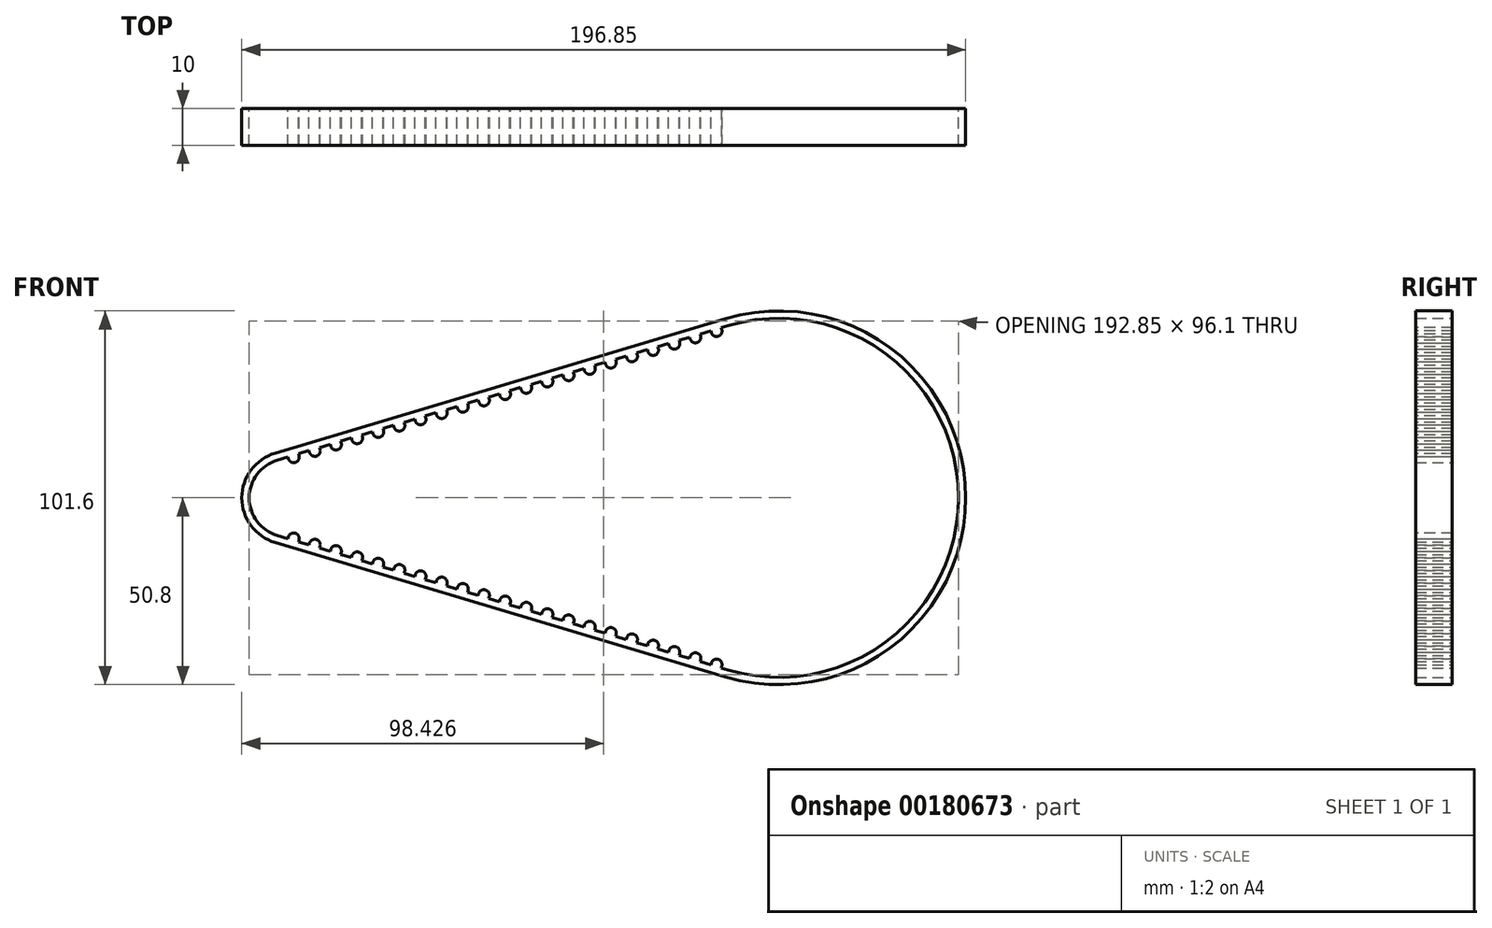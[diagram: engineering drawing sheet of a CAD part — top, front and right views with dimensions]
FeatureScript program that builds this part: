
annotation { "Feature Type Name" : "Feature", "Feature Type Description" : "" }
export const myFeature = defineFeature(function(context is Context, id is Id, definition is map)
    precondition{}
    {
        {
            var Q0;
            Q0=qCreatedBy(makeId("Front.planeOp"),FACE);
            var sketch = newSketch(context, id + "F0", { "sketchPlane" : qUnion([Q0])});
            skCircle(sketch, "E0", {"center": v(-282.88, 0) * mm, "radius": 30.69 * mm});
            skCircle(sketch, "E1", {"center": v(285.29, 0) * mm, "radius": 50.8 * mm});
            skLineSegment(sketch, "E2", {"start": v(-79.43, 12.17) * mm, "end": v(43.04, 48.68) * mm});
            skLineSegment(sketch, "E3", {"start": v(-79.43, -12.17) * mm, "end": v(43.04, -48.68) * mm});
            skArc(sketch, "E4", {"start": v(-79.43, 12.17) * mm, "mid": v(-88.5, 0) * mm, "end": v(-79.43, -12.17) * mm});
            skArc(sketch, "E5", {"start": v(43.04, -48.68) * mm, "mid": v(108.35, 0) * mm, "end": v(43.04, 48.68) * mm});
            skSolve(sketch);
        }
        {
            var Q0;
            Q0=makeQuery(id+"F0.imprint","IMPRINT",FACE,{"disambiguationData":[TD([[makeQuery(id+"F0.imprint","IMPRINT",EDGE,{"derivedFrom":sQuery(id+"F0.wireOp",EDGE,"E2")}),-1.0]])]});
            extrude(context, id + "F1", {"entities" : qUnion([Q0]), "depth" : 10 * mm});
        }
        {
            var Q0;
            Q0=makeQuery(id+"F1.opExtrude","CAP_FACE",FACE,{"disambiguationData":[OSD([sQuery(id+"F0.wireOp",EDGE,"E2"),sQuery(id+"F0.wireOp",EDGE,"E3"),sQuery(id+"F0.wireOp",EDGE,"E4"),sQuery(id+"F0.wireOp",EDGE,"E5")])],"isStart":false});
            var Q1;
            Q1=makeQuery(id+"F1.opExtrude","CAP_FACE",FACE,{"disambiguationData":[OSD([sQuery(id+"F0.wireOp",EDGE,"E2"),sQuery(id+"F0.wireOp",EDGE,"E3"),sQuery(id+"F0.wireOp",EDGE,"E4"),sQuery(id+"F0.wireOp",EDGE,"E5")])],"isStart":true});
            shell(context, id + "F2", {"entities" : qUnion([Q0, Q1]), "thickness" : 2 * mm});
        }
        {
            var Q0;
            Q0=makeQuery(id+"F1.opExtrude","SWEPT_FACE",FACE,{"disambiguationData":[OSD([sQuery(id+"F0.wireOp",EDGE,"E2")])]});
            var sketch = newSketch(context, id + "F3", { "sketchPlane" : qUnion([Q0])});
            skLineSegment(sketch, "E6", {"start": v(-69.64, 0) * mm, "end": v(-69.64, -10) * mm});
            skLineSegment(sketch, "E7", {"start": v(-72.64, -10) * mm, "end": v(-72.64, 0) * mm});
            skLineSegment(sketch, "E8", {"start": v(55.15, -10) * mm, "end": v(55.15, 0) * mm});
            skLineSegment(sketch, "E9.1.0.0", {"start": v(-66.64, 0) * mm, "end": v(-66.64, -10) * mm});
            skLineSegment(sketch, "E9.2.0.0", {"start": v(-63.64, 0) * mm, "end": v(-63.64, -10) * mm});
            skLineSegment(sketch, "E9.3.0.0", {"start": v(-60.64, 0) * mm, "end": v(-60.64, -10) * mm});
            skLineSegment(sketch, "E9.4.0.0", {"start": v(-57.64, 0) * mm, "end": v(-57.64, -10) * mm});
            skLineSegment(sketch, "E9.5.0.0", {"start": v(-54.64, 0) * mm, "end": v(-54.64, -10) * mm});
            skLineSegment(sketch, "E9.6.0.0", {"start": v(-51.64, 0) * mm, "end": v(-51.64, -10) * mm});
            skLineSegment(sketch, "E9.7.0.0", {"start": v(-48.64, 0) * mm, "end": v(-48.64, -10) * mm});
            skLineSegment(sketch, "E9.8.0.0", {"start": v(-45.64, 0) * mm, "end": v(-45.64, -10) * mm});
            skLineSegment(sketch, "E9.9.0.0", {"start": v(-42.64, 0) * mm, "end": v(-42.64, -10) * mm});
            skLineSegment(sketch, "E9.10.0.0", {"start": v(-39.64, 0) * mm, "end": v(-39.64, -10) * mm});
            skLineSegment(sketch, "E9.11.0.0", {"start": v(-36.64, 0) * mm, "end": v(-36.64, -10) * mm});
            skLineSegment(sketch, "E9.12.0.0", {"start": v(-33.64, 0) * mm, "end": v(-33.64, -10) * mm});
            skLineSegment(sketch, "E9.13.0.0", {"start": v(-30.64, 0) * mm, "end": v(-30.64, -10) * mm});
            skLineSegment(sketch, "E9.14.0.0", {"start": v(-27.64, 0) * mm, "end": v(-27.64, -10) * mm});
            skLineSegment(sketch, "E9.15.0.0", {"start": v(-24.64, 0) * mm, "end": v(-24.64, -10) * mm});
            skLineSegment(sketch, "E9.16.0.0", {"start": v(-21.64, 0) * mm, "end": v(-21.64, -10) * mm});
            skLineSegment(sketch, "E9.17.0.0", {"start": v(-18.64, 0) * mm, "end": v(-18.64, -10) * mm});
            skLineSegment(sketch, "E9.18.0.0", {"start": v(-15.64, 0) * mm, "end": v(-15.64, -10) * mm});
            skLineSegment(sketch, "E9.19.0.0", {"start": v(-12.64, 0) * mm, "end": v(-12.64, -10) * mm});
            skLineSegment(sketch, "E9.20.0.0", {"start": v(-9.64, 0) * mm, "end": v(-9.64, -10) * mm});
            skLineSegment(sketch, "E9.21.0.0", {"start": v(-6.64, 0) * mm, "end": v(-6.64, -10) * mm});
            skLineSegment(sketch, "E9.22.0.0", {"start": v(-3.64, 0) * mm, "end": v(-3.64, -10) * mm});
            skLineSegment(sketch, "E9.23.0.0", {"start": v(-0.64, 0) * mm, "end": v(-0.64, -10) * mm});
            skLineSegment(sketch, "E9.24.0.0", {"start": v(2.36, 0) * mm, "end": v(2.36, -10) * mm});
            skLineSegment(sketch, "E9.25.0.0", {"start": v(5.36, 0) * mm, "end": v(5.36, -10) * mm});
            skLineSegment(sketch, "E9.26.0.0", {"start": v(8.36, 0) * mm, "end": v(8.36, -10) * mm});
            skLineSegment(sketch, "E9.27.0.0", {"start": v(11.36, 0) * mm, "end": v(11.36, -10) * mm});
            skLineSegment(sketch, "E9.28.0.0", {"start": v(14.36, 0) * mm, "end": v(14.36, -10) * mm});
            skLineSegment(sketch, "E9.29.0.0", {"start": v(17.36, 0) * mm, "end": v(17.36, -10) * mm});
            skLineSegment(sketch, "E9.30.0.0", {"start": v(20.36, 0) * mm, "end": v(20.36, -10) * mm});
            skLineSegment(sketch, "E9.31.0.0", {"start": v(23.36, 0) * mm, "end": v(23.36, -10) * mm});
            skLineSegment(sketch, "E9.32.0.0", {"start": v(26.36, 0) * mm, "end": v(26.36, -10) * mm});
            skLineSegment(sketch, "E9.33.0.0", {"start": v(29.36, 0) * mm, "end": v(29.36, -10) * mm});
            skLineSegment(sketch, "E9.34.0.0", {"start": v(32.36, 0) * mm, "end": v(32.36, -10) * mm});
            skLineSegment(sketch, "E9.35.0.0", {"start": v(35.36, 0) * mm, "end": v(35.36, -10) * mm});
            skLineSegment(sketch, "E9.36.0.0", {"start": v(38.36, 0) * mm, "end": v(38.36, -10) * mm});
            skLineSegment(sketch, "E9.37.0.0", {"start": v(41.36, 0) * mm, "end": v(41.36, -10) * mm});
            skLineSegment(sketch, "E9.38.0.0", {"start": v(44.36, 0) * mm, "end": v(44.36, -10) * mm});
            skLineSegment(sketch, "E9.39.0.0", {"start": v(47.36, 0) * mm, "end": v(47.36, -10) * mm});
            skLineSegment(sketch, "E9.40.0.0", {"start": v(50.36, 0) * mm, "end": v(50.36, -10) * mm});
            skLineSegment(sketch, "E9.41.0.0", {"start": v(53.36, 0) * mm, "end": v(53.36, -10) * mm});
            skLineSegment(sketch, "E9.direction1", {"start": v(-69.64, -10) * mm, "end": v(-66.64, -10) * mm, "construction": true});
            skSolve(sketch);
        }
        {
            var Q0;
            {var subQ0=sQuery(id+"F3.wireOp",EDGE,"E6");Q0=makeQuery(id+"F3.imprint","IMPRINT",FACE,{"disambiguationData":[TD([[makeQuery(id+"F3.imprint","IMPRINT",EDGE,{"derivedFrom":subQ0}),1.0]])]});}
            var Q1;
            {var subQ0=sQuery(id+"F3.wireOp",EDGE,"E9.2.0.0");Q1=makeQuery(id+"F3.imprint","IMPRINT",FACE,{"disambiguationData":[TD([[makeQuery(id+"F3.imprint","IMPRINT",EDGE,{"derivedFrom":subQ0}),1.0]])]});}
            var Q2;
            {var subQ0=sQuery(id+"F3.wireOp",EDGE,"E9.4.0.0");Q2=makeQuery(id+"F3.imprint","IMPRINT",FACE,{"disambiguationData":[TD([[makeQuery(id+"F3.imprint","IMPRINT",EDGE,{"derivedFrom":subQ0}),1.0]])]});}
            var Q3;
            {var subQ0=sQuery(id+"F3.wireOp",EDGE,"E9.6.0.0");Q3=makeQuery(id+"F3.imprint","IMPRINT",FACE,{"disambiguationData":[TD([[makeQuery(id+"F3.imprint","IMPRINT",EDGE,{"derivedFrom":subQ0}),1.0]])]});}
            var Q4;
            {var subQ0=sQuery(id+"F3.wireOp",EDGE,"E9.8.0.0");Q4=makeQuery(id+"F3.imprint","IMPRINT",FACE,{"disambiguationData":[TD([[makeQuery(id+"F3.imprint","IMPRINT",EDGE,{"derivedFrom":subQ0}),1.0]])]});}
            var Q5;
            {var subQ0=sQuery(id+"F3.wireOp",EDGE,"E9.10.0.0");Q5=makeQuery(id+"F3.imprint","IMPRINT",FACE,{"disambiguationData":[TD([[makeQuery(id+"F3.imprint","IMPRINT",EDGE,{"derivedFrom":subQ0}),1.0]])]});}
            var Q6;
            {var subQ0=sQuery(id+"F3.wireOp",EDGE,"E9.12.0.0");Q6=makeQuery(id+"F3.imprint","IMPRINT",FACE,{"disambiguationData":[TD([[makeQuery(id+"F3.imprint","IMPRINT",EDGE,{"derivedFrom":subQ0}),1.0]])]});}
            var Q7;
            {var subQ0=sQuery(id+"F3.wireOp",EDGE,"E9.14.0.0");Q7=makeQuery(id+"F3.imprint","IMPRINT",FACE,{"disambiguationData":[TD([[makeQuery(id+"F3.imprint","IMPRINT",EDGE,{"derivedFrom":subQ0}),1.0]])]});}
            var Q8;
            {var subQ0=sQuery(id+"F3.wireOp",EDGE,"E9.16.0.0");Q8=makeQuery(id+"F3.imprint","IMPRINT",FACE,{"disambiguationData":[TD([[makeQuery(id+"F3.imprint","IMPRINT",EDGE,{"derivedFrom":subQ0}),1.0]])]});}
            var Q9;
            {var subQ0=sQuery(id+"F3.wireOp",EDGE,"E9.18.0.0");Q9=makeQuery(id+"F3.imprint","IMPRINT",FACE,{"disambiguationData":[TD([[makeQuery(id+"F3.imprint","IMPRINT",EDGE,{"derivedFrom":subQ0}),1.0]])]});}
            var Q10;
            {var subQ0=sQuery(id+"F3.wireOp",EDGE,"E9.20.0.0");Q10=makeQuery(id+"F3.imprint","IMPRINT",FACE,{"disambiguationData":[TD([[makeQuery(id+"F3.imprint","IMPRINT",EDGE,{"derivedFrom":subQ0}),1.0]])]});}
            var Q11;
            {var subQ0=sQuery(id+"F3.wireOp",EDGE,"E9.22.0.0");Q11=makeQuery(id+"F3.imprint","IMPRINT",FACE,{"disambiguationData":[TD([[makeQuery(id+"F3.imprint","IMPRINT",EDGE,{"derivedFrom":subQ0}),1.0]])]});}
            var Q12;
            {var subQ0=sQuery(id+"F3.wireOp",EDGE,"E9.24.0.0");Q12=makeQuery(id+"F3.imprint","IMPRINT",FACE,{"disambiguationData":[TD([[makeQuery(id+"F3.imprint","IMPRINT",EDGE,{"derivedFrom":subQ0}),1.0]])]});}
            var Q13;
            {var subQ0=sQuery(id+"F3.wireOp",EDGE,"E9.26.0.0");Q13=makeQuery(id+"F3.imprint","IMPRINT",FACE,{"disambiguationData":[TD([[makeQuery(id+"F3.imprint","IMPRINT",EDGE,{"derivedFrom":subQ0}),1.0]])]});}
            var Q14;
            {var subQ0=sQuery(id+"F3.wireOp",EDGE,"E9.28.0.0");Q14=makeQuery(id+"F3.imprint","IMPRINT",FACE,{"disambiguationData":[TD([[makeQuery(id+"F3.imprint","IMPRINT",EDGE,{"derivedFrom":subQ0}),1.0]])]});}
            var Q15;
            {var subQ0=sQuery(id+"F3.wireOp",EDGE,"E9.30.0.0");Q15=makeQuery(id+"F3.imprint","IMPRINT",FACE,{"disambiguationData":[TD([[makeQuery(id+"F3.imprint","IMPRINT",EDGE,{"derivedFrom":subQ0}),1.0]])]});}
            var Q16;
            {var subQ0=sQuery(id+"F3.wireOp",EDGE,"E9.32.0.0");Q16=makeQuery(id+"F3.imprint","IMPRINT",FACE,{"disambiguationData":[TD([[makeQuery(id+"F3.imprint","IMPRINT",EDGE,{"derivedFrom":subQ0}),1.0]])]});}
            var Q17;
            {var subQ0=sQuery(id+"F3.wireOp",EDGE,"E9.34.0.0");Q17=makeQuery(id+"F3.imprint","IMPRINT",FACE,{"disambiguationData":[TD([[makeQuery(id+"F3.imprint","IMPRINT",EDGE,{"derivedFrom":subQ0}),1.0]])]});}
            var Q18;
            {var subQ0=sQuery(id+"F3.wireOp",EDGE,"E9.36.0.0");Q18=makeQuery(id+"F3.imprint","IMPRINT",FACE,{"disambiguationData":[TD([[makeQuery(id+"F3.imprint","IMPRINT",EDGE,{"derivedFrom":subQ0}),1.0]])]});}
            var Q19;
            {var subQ0=sQuery(id+"F3.wireOp",EDGE,"E9.38.0.0");Q19=makeQuery(id+"F3.imprint","IMPRINT",FACE,{"disambiguationData":[TD([[makeQuery(id+"F3.imprint","IMPRINT",EDGE,{"derivedFrom":subQ0}),1.0]])]});}
            var Q20;
            {var subQ0=sQuery(id+"F3.wireOp",EDGE,"E9.40.0.0");Q20=makeQuery(id+"F3.imprint","IMPRINT",FACE,{"disambiguationData":[TD([[makeQuery(id+"F3.imprint","IMPRINT",EDGE,{"derivedFrom":subQ0}),1.0]])]});}
            extrude(context, id + "F4", {"entities" : qUnion([Q0, Q1, Q2, Q3, Q4, Q5, Q6, Q7, Q8, Q9, Q10, Q11, Q12, Q13, Q14, Q15, Q16, Q17, Q18, Q19, Q20]), "operationType" : NewBodyOperationType.ADD, "oppositeDirection" : true, "depth" : 4 * mm});
        }
        {
            var Q0;
            Q0=makeQuery(id+"F4.opExtrude","CAP_EDGE",EDGE,{"disambiguationData":[OSD([sQuery(id+"F3.wireOp",EDGE,"E6")])],"isStart":false});
            fillet(context, id + "F5", {"entities" : qUnion([Q0]), "radius" : 1.5 * mm, "tangentPropagation" : true, "allowEdgeOverflow" : false});
        }
        {
            var Q0;
            Q0=makeQuery(id+"F4.opExtrude","CAP_EDGE",EDGE,{"disambiguationData":[OSD([sQuery(id+"F3.wireOp",EDGE,"E9.1.0.0")])],"isStart":false});
            var Q1;
            Q1=makeQuery(id+"F4.opExtrude","CAP_EDGE",EDGE,{"disambiguationData":[OSD([sQuery(id+"F3.wireOp",EDGE,"E9.2.0.0")])],"isStart":false});
            var Q2;
            Q2=makeQuery(id+"F4.opExtrude","CAP_EDGE",EDGE,{"disambiguationData":[OSD([sQuery(id+"F3.wireOp",EDGE,"E9.3.0.0")])],"isStart":false});
            var Q3;
            Q3=makeQuery(id+"F4.opExtrude","CAP_EDGE",EDGE,{"disambiguationData":[OSD([sQuery(id+"F3.wireOp",EDGE,"E9.4.0.0")])],"isStart":false});
            var Q4;
            Q4=makeQuery(id+"F4.opExtrude","CAP_EDGE",EDGE,{"disambiguationData":[OSD([sQuery(id+"F3.wireOp",EDGE,"E9.5.0.0")])],"isStart":false});
            var Q5;
            Q5=makeQuery(id+"F4.opExtrude","CAP_EDGE",EDGE,{"disambiguationData":[OSD([sQuery(id+"F3.wireOp",EDGE,"E9.6.0.0")])],"isStart":false});
            var Q6;
            Q6=makeQuery(id+"F4.opExtrude","CAP_EDGE",EDGE,{"disambiguationData":[OSD([sQuery(id+"F3.wireOp",EDGE,"E9.7.0.0")])],"isStart":false});
            var Q7;
            Q7=makeQuery(id+"F4.opExtrude","CAP_EDGE",EDGE,{"disambiguationData":[OSD([sQuery(id+"F3.wireOp",EDGE,"E9.8.0.0")])],"isStart":false});
            var Q8;
            Q8=makeQuery(id+"F4.opExtrude","CAP_EDGE",EDGE,{"disambiguationData":[OSD([sQuery(id+"F3.wireOp",EDGE,"E9.9.0.0")])],"isStart":false});
            var Q9;
            Q9=makeQuery(id+"F4.opExtrude","CAP_EDGE",EDGE,{"disambiguationData":[OSD([sQuery(id+"F3.wireOp",EDGE,"E9.10.0.0")])],"isStart":false});
            var Q10;
            Q10=makeQuery(id+"F4.opExtrude","CAP_EDGE",EDGE,{"disambiguationData":[OSD([sQuery(id+"F3.wireOp",EDGE,"E9.11.0.0")])],"isStart":false});
            var Q11;
            Q11=makeQuery(id+"F4.opExtrude","CAP_EDGE",EDGE,{"disambiguationData":[OSD([sQuery(id+"F3.wireOp",EDGE,"E9.12.0.0")])],"isStart":false});
            var Q12;
            Q12=makeQuery(id+"F4.opExtrude","CAP_EDGE",EDGE,{"disambiguationData":[OSD([sQuery(id+"F3.wireOp",EDGE,"E9.13.0.0")])],"isStart":false});
            var Q13;
            Q13=makeQuery(id+"F4.opExtrude","CAP_EDGE",EDGE,{"disambiguationData":[OSD([sQuery(id+"F3.wireOp",EDGE,"E9.14.0.0")])],"isStart":false});
            var Q14;
            Q14=makeQuery(id+"F4.opExtrude","CAP_EDGE",EDGE,{"disambiguationData":[OSD([sQuery(id+"F3.wireOp",EDGE,"E9.15.0.0")])],"isStart":false});
            var Q15;
            Q15=makeQuery(id+"F4.opExtrude","CAP_EDGE",EDGE,{"disambiguationData":[OSD([sQuery(id+"F3.wireOp",EDGE,"E9.16.0.0")])],"isStart":false});
            var Q16;
            Q16=makeQuery(id+"F4.opExtrude","CAP_EDGE",EDGE,{"disambiguationData":[OSD([sQuery(id+"F3.wireOp",EDGE,"E9.17.0.0")])],"isStart":false});
            var Q17;
            Q17=makeQuery(id+"F4.opExtrude","CAP_EDGE",EDGE,{"disambiguationData":[OSD([sQuery(id+"F3.wireOp",EDGE,"E9.18.0.0")])],"isStart":false});
            var Q18;
            Q18=makeQuery(id+"F4.opExtrude","CAP_EDGE",EDGE,{"disambiguationData":[OSD([sQuery(id+"F3.wireOp",EDGE,"E9.19.0.0")])],"isStart":false});
            var Q19;
            Q19=makeQuery(id+"F4.opExtrude","CAP_EDGE",EDGE,{"disambiguationData":[OSD([sQuery(id+"F3.wireOp",EDGE,"E9.20.0.0")])],"isStart":false});
            var Q20;
            Q20=makeQuery(id+"F4.opExtrude","CAP_EDGE",EDGE,{"disambiguationData":[OSD([sQuery(id+"F3.wireOp",EDGE,"E9.21.0.0")])],"isStart":false});
            var Q21;
            Q21=makeQuery(id+"F4.opExtrude","CAP_EDGE",EDGE,{"disambiguationData":[OSD([sQuery(id+"F3.wireOp",EDGE,"E9.22.0.0")])],"isStart":false});
            var Q22;
            Q22=makeQuery(id+"F4.opExtrude","CAP_EDGE",EDGE,{"disambiguationData":[OSD([sQuery(id+"F3.wireOp",EDGE,"E9.23.0.0")])],"isStart":false});
            var Q23;
            Q23=makeQuery(id+"F4.opExtrude","CAP_EDGE",EDGE,{"disambiguationData":[OSD([sQuery(id+"F3.wireOp",EDGE,"E9.24.0.0")])],"isStart":false});
            var Q24;
            Q24=makeQuery(id+"F4.opExtrude","CAP_EDGE",EDGE,{"disambiguationData":[OSD([sQuery(id+"F3.wireOp",EDGE,"E9.25.0.0")])],"isStart":false});
            var Q25;
            Q25=makeQuery(id+"F4.opExtrude","CAP_EDGE",EDGE,{"disambiguationData":[OSD([sQuery(id+"F3.wireOp",EDGE,"E9.26.0.0")])],"isStart":false});
            var Q26;
            Q26=makeQuery(id+"F4.opExtrude","CAP_EDGE",EDGE,{"disambiguationData":[OSD([sQuery(id+"F3.wireOp",EDGE,"E9.27.0.0")])],"isStart":false});
            var Q27;
            Q27=makeQuery(id+"F4.opExtrude","CAP_EDGE",EDGE,{"disambiguationData":[OSD([sQuery(id+"F3.wireOp",EDGE,"E9.28.0.0")])],"isStart":false});
            var Q28;
            Q28=makeQuery(id+"F4.opExtrude","CAP_EDGE",EDGE,{"disambiguationData":[OSD([sQuery(id+"F3.wireOp",EDGE,"E9.29.0.0")])],"isStart":false});
            var Q29;
            Q29=makeQuery(id+"F4.opExtrude","CAP_EDGE",EDGE,{"disambiguationData":[OSD([sQuery(id+"F3.wireOp",EDGE,"E9.30.0.0")])],"isStart":false});
            var Q30;
            Q30=makeQuery(id+"F4.opExtrude","CAP_EDGE",EDGE,{"disambiguationData":[OSD([sQuery(id+"F3.wireOp",EDGE,"E9.31.0.0")])],"isStart":false});
            var Q31;
            Q31=makeQuery(id+"F4.opExtrude","CAP_EDGE",EDGE,{"disambiguationData":[OSD([sQuery(id+"F3.wireOp",EDGE,"E9.32.0.0")])],"isStart":false});
            var Q32;
            Q32=makeQuery(id+"F4.opExtrude","CAP_EDGE",EDGE,{"disambiguationData":[OSD([sQuery(id+"F3.wireOp",EDGE,"E9.33.0.0")])],"isStart":false});
            var Q33;
            Q33=makeQuery(id+"F4.opExtrude","CAP_EDGE",EDGE,{"disambiguationData":[OSD([sQuery(id+"F3.wireOp",EDGE,"E9.34.0.0")])],"isStart":false});
            var Q34;
            Q34=makeQuery(id+"F4.opExtrude","CAP_EDGE",EDGE,{"disambiguationData":[OSD([sQuery(id+"F3.wireOp",EDGE,"E9.35.0.0")])],"isStart":false});
            var Q35;
            Q35=makeQuery(id+"F4.opExtrude","CAP_EDGE",EDGE,{"disambiguationData":[OSD([sQuery(id+"F3.wireOp",EDGE,"E9.36.0.0")])],"isStart":false});
            var Q36;
            Q36=makeQuery(id+"F4.opExtrude","CAP_EDGE",EDGE,{"disambiguationData":[OSD([sQuery(id+"F3.wireOp",EDGE,"E9.37.0.0")])],"isStart":false});
            var Q37;
            Q37=makeQuery(id+"F4.opExtrude","CAP_EDGE",EDGE,{"disambiguationData":[OSD([sQuery(id+"F3.wireOp",EDGE,"E9.38.0.0")])],"isStart":false});
            var Q38;
            Q38=makeQuery(id+"F4.opExtrude","CAP_EDGE",EDGE,{"disambiguationData":[OSD([sQuery(id+"F3.wireOp",EDGE,"E9.39.0.0")])],"isStart":false});
            var Q39;
            Q39=makeQuery(id+"F4.opExtrude","CAP_EDGE",EDGE,{"disambiguationData":[OSD([sQuery(id+"F3.wireOp",EDGE,"E9.40.0.0")])],"isStart":false});
            var Q40;
            Q40=makeQuery(id+"F4.opExtrude","CAP_EDGE",EDGE,{"disambiguationData":[OSD([sQuery(id+"F3.wireOp",EDGE,"E9.41.0.0")])],"isStart":false});
            fillet(context, id + "F6", {"entities" : qUnion([Q0, Q1, Q2, Q3, Q4, Q5, Q6, Q7, Q8, Q9, Q10, Q11, Q12, Q13, Q14, Q15, Q16, Q17, Q18, Q19, Q20, Q21, Q22, Q23, Q24, Q25, Q26, Q27, Q28, Q29, Q30, Q31, Q32, Q33, Q34, Q35, Q36, Q37, Q38, Q39, Q40]), "radius" : 1.5 * mm, "tangentPropagation" : true, "allowEdgeOverflow" : false});
        }
        {
            var Q0;
            Q0=makeQuery(id+"F1.opExtrude","SWEPT_FACE",FACE,{"disambiguationData":[OSD([sQuery(id+"F0.wireOp",EDGE,"E3")])]});
            var sketch = newSketch(context, id + "F7", { "sketchPlane" : qUnion([Q0])});
            skLineSegment(sketch, "E10", {"start": v(-72.64, 0) * mm, "end": v(-72.64, 10) * mm});
            skLineSegment(sketch, "E11", {"start": v(-69.64, 0) * mm, "end": v(-69.64, 10) * mm});
            skLineSegment(sketch, "E12.1.0.0", {"start": v(-66.64, 0) * mm, "end": v(-66.64, 10) * mm});
            skLineSegment(sketch, "E12.2.0.0", {"start": v(-63.64, 0) * mm, "end": v(-63.64, 10) * mm});
            skLineSegment(sketch, "E12.3.0.0", {"start": v(-60.64, 0) * mm, "end": v(-60.64, 10) * mm});
            skLineSegment(sketch, "E12.4.0.0", {"start": v(-57.64, 0) * mm, "end": v(-57.64, 10) * mm});
            skLineSegment(sketch, "E12.5.0.0", {"start": v(-54.64, 0) * mm, "end": v(-54.64, 10) * mm});
            skLineSegment(sketch, "E12.6.0.0", {"start": v(-51.64, 0) * mm, "end": v(-51.64, 10) * mm});
            skLineSegment(sketch, "E12.7.0.0", {"start": v(-48.64, 0) * mm, "end": v(-48.64, 10) * mm});
            skLineSegment(sketch, "E12.8.0.0", {"start": v(-45.64, 0) * mm, "end": v(-45.64, 10) * mm});
            skLineSegment(sketch, "E12.9.0.0", {"start": v(-42.64, 0) * mm, "end": v(-42.64, 10) * mm});
            skLineSegment(sketch, "E12.10.0.0", {"start": v(-39.64, 0) * mm, "end": v(-39.64, 10) * mm});
            skLineSegment(sketch, "E12.11.0.0", {"start": v(-36.64, 0) * mm, "end": v(-36.64, 10) * mm});
            skLineSegment(sketch, "E12.12.0.0", {"start": v(-33.64, 0) * mm, "end": v(-33.64, 10) * mm});
            skLineSegment(sketch, "E12.13.0.0", {"start": v(-30.64, 0) * mm, "end": v(-30.64, 10) * mm});
            skLineSegment(sketch, "E12.14.0.0", {"start": v(-27.64, 0) * mm, "end": v(-27.64, 10) * mm});
            skLineSegment(sketch, "E12.15.0.0", {"start": v(-24.64, 0) * mm, "end": v(-24.64, 10) * mm});
            skLineSegment(sketch, "E12.16.0.0", {"start": v(-21.64, 0) * mm, "end": v(-21.64, 10) * mm});
            skLineSegment(sketch, "E12.17.0.0", {"start": v(-18.64, 0) * mm, "end": v(-18.64, 10) * mm});
            skLineSegment(sketch, "E12.18.0.0", {"start": v(-15.64, 0) * mm, "end": v(-15.64, 10) * mm});
            skLineSegment(sketch, "E12.19.0.0", {"start": v(-12.64, 0) * mm, "end": v(-12.64, 10) * mm});
            skLineSegment(sketch, "E12.20.0.0", {"start": v(-9.64, 0) * mm, "end": v(-9.64, 10) * mm});
            skLineSegment(sketch, "E12.21.0.0", {"start": v(-6.64, 0) * mm, "end": v(-6.64, 10) * mm});
            skLineSegment(sketch, "E12.22.0.0", {"start": v(-3.64, 0) * mm, "end": v(-3.64, 10) * mm});
            skLineSegment(sketch, "E12.23.0.0", {"start": v(-0.64, 0) * mm, "end": v(-0.64, 10) * mm});
            skLineSegment(sketch, "E12.24.0.0", {"start": v(2.36, 0) * mm, "end": v(2.36, 10) * mm});
            skLineSegment(sketch, "E12.25.0.0", {"start": v(5.36, 0) * mm, "end": v(5.36, 10) * mm});
            skLineSegment(sketch, "E12.26.0.0", {"start": v(8.36, 0) * mm, "end": v(8.36, 10) * mm});
            skLineSegment(sketch, "E12.27.0.0", {"start": v(11.36, 0) * mm, "end": v(11.36, 10) * mm});
            skLineSegment(sketch, "E12.28.0.0", {"start": v(14.36, 0) * mm, "end": v(14.36, 10) * mm});
            skLineSegment(sketch, "E12.29.0.0", {"start": v(17.36, 0) * mm, "end": v(17.36, 10) * mm});
            skLineSegment(sketch, "E12.30.0.0", {"start": v(20.36, 0) * mm, "end": v(20.36, 10) * mm});
            skLineSegment(sketch, "E12.31.0.0", {"start": v(23.36, 0) * mm, "end": v(23.36, 10) * mm});
            skLineSegment(sketch, "E12.32.0.0", {"start": v(26.36, 0) * mm, "end": v(26.36, 10) * mm});
            skLineSegment(sketch, "E12.33.0.0", {"start": v(29.36, 0) * mm, "end": v(29.36, 10) * mm});
            skLineSegment(sketch, "E12.34.0.0", {"start": v(32.36, 0) * mm, "end": v(32.36, 10) * mm});
            skLineSegment(sketch, "E12.35.0.0", {"start": v(35.36, 0) * mm, "end": v(35.36, 10) * mm});
            skLineSegment(sketch, "E12.36.0.0", {"start": v(38.36, 0) * mm, "end": v(38.36, 10) * mm});
            skLineSegment(sketch, "E12.37.0.0", {"start": v(41.36, 0) * mm, "end": v(41.36, 10) * mm});
            skLineSegment(sketch, "E12.38.0.0", {"start": v(44.36, 0) * mm, "end": v(44.36, 10) * mm});
            skLineSegment(sketch, "E12.39.0.0", {"start": v(47.36, 0) * mm, "end": v(47.36, 10) * mm});
            skLineSegment(sketch, "E12.40.0.0", {"start": v(50.36, 0) * mm, "end": v(50.36, 10) * mm});
            skLineSegment(sketch, "E12.41.0.0", {"start": v(53.36, 0) * mm, "end": v(53.36, 10) * mm});
            skLineSegment(sketch, "E12.direction1", {"start": v(-69.64, 0) * mm, "end": v(-66.64, 0) * mm, "construction": true});
            skSolve(sketch);
        }
        {
            var Q0;
            {var subQ0=sQuery(id+"F7.wireOp",EDGE,"E11");Q0=makeQuery(id+"F7.imprint","IMPRINT",FACE,{"disambiguationData":[TD([[makeQuery(id+"F7.imprint","IMPRINT",EDGE,{"derivedFrom":subQ0}),-1.0]])]});}
            var Q1;
            {var subQ0=sQuery(id+"F7.wireOp",EDGE,"E12.2.0.0");Q1=makeQuery(id+"F7.imprint","IMPRINT",FACE,{"disambiguationData":[TD([[makeQuery(id+"F7.imprint","IMPRINT",EDGE,{"derivedFrom":subQ0}),-1.0]])]});}
            var Q2;
            {var subQ0=sQuery(id+"F7.wireOp",EDGE,"E12.4.0.0");Q2=makeQuery(id+"F7.imprint","IMPRINT",FACE,{"disambiguationData":[TD([[makeQuery(id+"F7.imprint","IMPRINT",EDGE,{"derivedFrom":subQ0}),-1.0]])]});}
            var Q3;
            {var subQ0=sQuery(id+"F7.wireOp",EDGE,"E12.6.0.0");Q3=makeQuery(id+"F7.imprint","IMPRINT",FACE,{"disambiguationData":[TD([[makeQuery(id+"F7.imprint","IMPRINT",EDGE,{"derivedFrom":subQ0}),-1.0]])]});}
            var Q4;
            {var subQ0=sQuery(id+"F7.wireOp",EDGE,"E12.8.0.0");Q4=makeQuery(id+"F7.imprint","IMPRINT",FACE,{"disambiguationData":[TD([[makeQuery(id+"F7.imprint","IMPRINT",EDGE,{"derivedFrom":subQ0}),-1.0]])]});}
            var Q5;
            {var subQ0=sQuery(id+"F7.wireOp",EDGE,"E12.10.0.0");Q5=makeQuery(id+"F7.imprint","IMPRINT",FACE,{"disambiguationData":[TD([[makeQuery(id+"F7.imprint","IMPRINT",EDGE,{"derivedFrom":subQ0}),-1.0]])]});}
            var Q6;
            {var subQ0=sQuery(id+"F7.wireOp",EDGE,"E12.12.0.0");Q6=makeQuery(id+"F7.imprint","IMPRINT",FACE,{"disambiguationData":[TD([[makeQuery(id+"F7.imprint","IMPRINT",EDGE,{"derivedFrom":subQ0}),-1.0]])]});}
            var Q7;
            {var subQ0=sQuery(id+"F7.wireOp",EDGE,"E12.14.0.0");Q7=makeQuery(id+"F7.imprint","IMPRINT",FACE,{"disambiguationData":[TD([[makeQuery(id+"F7.imprint","IMPRINT",EDGE,{"derivedFrom":subQ0}),-1.0]])]});}
            var Q8;
            {var subQ0=sQuery(id+"F7.wireOp",EDGE,"E12.16.0.0");Q8=makeQuery(id+"F7.imprint","IMPRINT",FACE,{"disambiguationData":[TD([[makeQuery(id+"F7.imprint","IMPRINT",EDGE,{"derivedFrom":subQ0}),-1.0]])]});}
            var Q9;
            {var subQ0=sQuery(id+"F7.wireOp",EDGE,"E12.18.0.0");Q9=makeQuery(id+"F7.imprint","IMPRINT",FACE,{"disambiguationData":[TD([[makeQuery(id+"F7.imprint","IMPRINT",EDGE,{"derivedFrom":subQ0}),-1.0]])]});}
            var Q10;
            {var subQ0=sQuery(id+"F7.wireOp",EDGE,"E12.20.0.0");Q10=makeQuery(id+"F7.imprint","IMPRINT",FACE,{"disambiguationData":[TD([[makeQuery(id+"F7.imprint","IMPRINT",EDGE,{"derivedFrom":subQ0}),-1.0]])]});}
            var Q11;
            {var subQ0=sQuery(id+"F7.wireOp",EDGE,"E12.22.0.0");Q11=makeQuery(id+"F7.imprint","IMPRINT",FACE,{"disambiguationData":[TD([[makeQuery(id+"F7.imprint","IMPRINT",EDGE,{"derivedFrom":subQ0}),-1.0]])]});}
            var Q12;
            {var subQ0=sQuery(id+"F7.wireOp",EDGE,"E12.24.0.0");Q12=makeQuery(id+"F7.imprint","IMPRINT",FACE,{"disambiguationData":[TD([[makeQuery(id+"F7.imprint","IMPRINT",EDGE,{"derivedFrom":subQ0}),-1.0]])]});}
            var Q13;
            {var subQ0=sQuery(id+"F7.wireOp",EDGE,"E12.26.0.0");Q13=makeQuery(id+"F7.imprint","IMPRINT",FACE,{"disambiguationData":[TD([[makeQuery(id+"F7.imprint","IMPRINT",EDGE,{"derivedFrom":subQ0}),-1.0]])]});}
            var Q14;
            {var subQ0=sQuery(id+"F7.wireOp",EDGE,"E12.28.0.0");Q14=makeQuery(id+"F7.imprint","IMPRINT",FACE,{"disambiguationData":[TD([[makeQuery(id+"F7.imprint","IMPRINT",EDGE,{"derivedFrom":subQ0}),-1.0]])]});}
            var Q15;
            {var subQ0=sQuery(id+"F7.wireOp",EDGE,"E12.30.0.0");Q15=makeQuery(id+"F7.imprint","IMPRINT",FACE,{"disambiguationData":[TD([[makeQuery(id+"F7.imprint","IMPRINT",EDGE,{"derivedFrom":subQ0}),-1.0]])]});}
            var Q16;
            {var subQ0=sQuery(id+"F7.wireOp",EDGE,"E12.32.0.0");Q16=makeQuery(id+"F7.imprint","IMPRINT",FACE,{"disambiguationData":[TD([[makeQuery(id+"F7.imprint","IMPRINT",EDGE,{"derivedFrom":subQ0}),-1.0]])]});}
            var Q17;
            {var subQ0=sQuery(id+"F7.wireOp",EDGE,"E12.34.0.0");Q17=makeQuery(id+"F7.imprint","IMPRINT",FACE,{"disambiguationData":[TD([[makeQuery(id+"F7.imprint","IMPRINT",EDGE,{"derivedFrom":subQ0}),-1.0]])]});}
            var Q18;
            {var subQ0=sQuery(id+"F7.wireOp",EDGE,"E12.36.0.0");Q18=makeQuery(id+"F7.imprint","IMPRINT",FACE,{"disambiguationData":[TD([[makeQuery(id+"F7.imprint","IMPRINT",EDGE,{"derivedFrom":subQ0}),-1.0]])]});}
            var Q19;
            {var subQ0=sQuery(id+"F7.wireOp",EDGE,"E12.38.0.0");Q19=makeQuery(id+"F7.imprint","IMPRINT",FACE,{"disambiguationData":[TD([[makeQuery(id+"F7.imprint","IMPRINT",EDGE,{"derivedFrom":subQ0}),-1.0]])]});}
            var Q20;
            {var subQ0=sQuery(id+"F7.wireOp",EDGE,"E12.40.0.0");Q20=makeQuery(id+"F7.imprint","IMPRINT",FACE,{"disambiguationData":[TD([[makeQuery(id+"F7.imprint","IMPRINT",EDGE,{"derivedFrom":subQ0}),-1.0]])]});}
            extrude(context, id + "F8", {"entities" : qUnion([Q0, Q1, Q2, Q3, Q4, Q5, Q6, Q7, Q8, Q9, Q10, Q11, Q12, Q13, Q14, Q15, Q16, Q17, Q18, Q19, Q20]), "operationType" : NewBodyOperationType.ADD, "oppositeDirection" : true, "depth" : 4 * mm});
        }
        {
            var Q0;
            Q0=makeQuery(id+"F8.opExtrude","CAP_EDGE",EDGE,{"disambiguationData":[OSD([sQuery(id+"F7.wireOp",EDGE,"E11")])],"isStart":false});
            var Q1;
            Q1=makeQuery(id+"F8.opExtrude","CAP_EDGE",EDGE,{"disambiguationData":[OSD([sQuery(id+"F7.wireOp",EDGE,"E12.1.0.0")])],"isStart":false});
            var Q2;
            Q2=makeQuery(id+"F8.opExtrude","CAP_EDGE",EDGE,{"disambiguationData":[OSD([sQuery(id+"F7.wireOp",EDGE,"E12.2.0.0")])],"isStart":false});
            var Q3;
            Q3=makeQuery(id+"F8.opExtrude","CAP_EDGE",EDGE,{"disambiguationData":[OSD([sQuery(id+"F7.wireOp",EDGE,"E12.3.0.0")])],"isStart":false});
            var Q4;
            Q4=makeQuery(id+"F8.opExtrude","CAP_EDGE",EDGE,{"disambiguationData":[OSD([sQuery(id+"F7.wireOp",EDGE,"E12.4.0.0")])],"isStart":false});
            var Q5;
            Q5=makeQuery(id+"F8.opExtrude","CAP_EDGE",EDGE,{"disambiguationData":[OSD([sQuery(id+"F7.wireOp",EDGE,"E12.6.0.0")])],"isStart":false});
            var Q6;
            Q6=makeQuery(id+"F8.opExtrude","CAP_EDGE",EDGE,{"disambiguationData":[OSD([sQuery(id+"F7.wireOp",EDGE,"E12.5.0.0")])],"isStart":false});
            var Q7;
            Q7=makeQuery(id+"F8.opExtrude","CAP_EDGE",EDGE,{"disambiguationData":[OSD([sQuery(id+"F7.wireOp",EDGE,"E12.7.0.0")])],"isStart":false});
            var Q8;
            Q8=makeQuery(id+"F8.opExtrude","CAP_EDGE",EDGE,{"disambiguationData":[OSD([sQuery(id+"F7.wireOp",EDGE,"E12.8.0.0")])],"isStart":false});
            var Q9;
            Q9=makeQuery(id+"F8.opExtrude","CAP_EDGE",EDGE,{"disambiguationData":[OSD([sQuery(id+"F7.wireOp",EDGE,"E12.9.0.0")])],"isStart":false});
            var Q10;
            Q10=makeQuery(id+"F8.opExtrude","CAP_EDGE",EDGE,{"disambiguationData":[OSD([sQuery(id+"F7.wireOp",EDGE,"E12.10.0.0")])],"isStart":false});
            var Q11;
            Q11=makeQuery(id+"F8.opExtrude","CAP_EDGE",EDGE,{"disambiguationData":[OSD([sQuery(id+"F7.wireOp",EDGE,"E12.11.0.0")])],"isStart":false});
            var Q12;
            Q12=makeQuery(id+"F8.opExtrude","CAP_EDGE",EDGE,{"disambiguationData":[OSD([sQuery(id+"F7.wireOp",EDGE,"E12.12.0.0")])],"isStart":false});
            var Q13;
            Q13=makeQuery(id+"F8.opExtrude","CAP_EDGE",EDGE,{"disambiguationData":[OSD([sQuery(id+"F7.wireOp",EDGE,"E12.13.0.0")])],"isStart":false});
            var Q14;
            Q14=makeQuery(id+"F8.opExtrude","CAP_EDGE",EDGE,{"disambiguationData":[OSD([sQuery(id+"F7.wireOp",EDGE,"E12.14.0.0")])],"isStart":false});
            var Q15;
            Q15=makeQuery(id+"F8.opExtrude","CAP_EDGE",EDGE,{"disambiguationData":[OSD([sQuery(id+"F7.wireOp",EDGE,"E12.15.0.0")])],"isStart":false});
            var Q16;
            Q16=makeQuery(id+"F8.opExtrude","CAP_EDGE",EDGE,{"disambiguationData":[OSD([sQuery(id+"F7.wireOp",EDGE,"E12.16.0.0")])],"isStart":false});
            var Q17;
            Q17=makeQuery(id+"F8.opExtrude","CAP_EDGE",EDGE,{"disambiguationData":[OSD([sQuery(id+"F7.wireOp",EDGE,"E12.17.0.0")])],"isStart":false});
            var Q18;
            Q18=makeQuery(id+"F8.opExtrude","CAP_EDGE",EDGE,{"disambiguationData":[OSD([sQuery(id+"F7.wireOp",EDGE,"E12.18.0.0")])],"isStart":false});
            var Q19;
            Q19=makeQuery(id+"F8.opExtrude","CAP_EDGE",EDGE,{"disambiguationData":[OSD([sQuery(id+"F7.wireOp",EDGE,"E12.19.0.0")])],"isStart":false});
            var Q20;
            Q20=makeQuery(id+"F8.opExtrude","CAP_EDGE",EDGE,{"disambiguationData":[OSD([sQuery(id+"F7.wireOp",EDGE,"E12.20.0.0")])],"isStart":false});
            var Q21;
            Q21=makeQuery(id+"F8.opExtrude","CAP_EDGE",EDGE,{"disambiguationData":[OSD([sQuery(id+"F7.wireOp",EDGE,"E12.21.0.0")])],"isStart":false});
            var Q22;
            Q22=makeQuery(id+"F8.opExtrude","CAP_EDGE",EDGE,{"disambiguationData":[OSD([sQuery(id+"F7.wireOp",EDGE,"E12.22.0.0")])],"isStart":false});
            var Q23;
            Q23=makeQuery(id+"F8.opExtrude","CAP_EDGE",EDGE,{"disambiguationData":[OSD([sQuery(id+"F7.wireOp",EDGE,"E12.23.0.0")])],"isStart":false});
            var Q24;
            Q24=makeQuery(id+"F8.opExtrude","CAP_EDGE",EDGE,{"disambiguationData":[OSD([sQuery(id+"F7.wireOp",EDGE,"E12.24.0.0")])],"isStart":false});
            var Q25;
            Q25=makeQuery(id+"F8.opExtrude","CAP_EDGE",EDGE,{"disambiguationData":[OSD([sQuery(id+"F7.wireOp",EDGE,"E12.25.0.0")])],"isStart":false});
            var Q26;
            Q26=makeQuery(id+"F8.opExtrude","CAP_EDGE",EDGE,{"disambiguationData":[OSD([sQuery(id+"F7.wireOp",EDGE,"E12.26.0.0")])],"isStart":false});
            var Q27;
            Q27=makeQuery(id+"F8.opExtrude","CAP_EDGE",EDGE,{"disambiguationData":[OSD([sQuery(id+"F7.wireOp",EDGE,"E12.27.0.0")])],"isStart":false});
            var Q28;
            Q28=makeQuery(id+"F8.opExtrude","CAP_EDGE",EDGE,{"disambiguationData":[OSD([sQuery(id+"F7.wireOp",EDGE,"E12.28.0.0")])],"isStart":false});
            var Q29;
            Q29=makeQuery(id+"F8.opExtrude","CAP_EDGE",EDGE,{"disambiguationData":[OSD([sQuery(id+"F7.wireOp",EDGE,"E12.29.0.0")])],"isStart":false});
            var Q30;
            Q30=makeQuery(id+"F8.opExtrude","CAP_EDGE",EDGE,{"disambiguationData":[OSD([sQuery(id+"F7.wireOp",EDGE,"E12.30.0.0")])],"isStart":false});
            var Q31;
            Q31=makeQuery(id+"F8.opExtrude","CAP_EDGE",EDGE,{"disambiguationData":[OSD([sQuery(id+"F7.wireOp",EDGE,"E12.31.0.0")])],"isStart":false});
            var Q32;
            Q32=makeQuery(id+"F8.opExtrude","CAP_EDGE",EDGE,{"disambiguationData":[OSD([sQuery(id+"F7.wireOp",EDGE,"E12.32.0.0")])],"isStart":false});
            var Q33;
            Q33=makeQuery(id+"F8.opExtrude","CAP_EDGE",EDGE,{"disambiguationData":[OSD([sQuery(id+"F7.wireOp",EDGE,"E12.33.0.0")])],"isStart":false});
            var Q34;
            Q34=makeQuery(id+"F8.opExtrude","CAP_EDGE",EDGE,{"disambiguationData":[OSD([sQuery(id+"F7.wireOp",EDGE,"E12.34.0.0")])],"isStart":false});
            var Q35;
            Q35=makeQuery(id+"F8.opExtrude","CAP_EDGE",EDGE,{"disambiguationData":[OSD([sQuery(id+"F7.wireOp",EDGE,"E12.35.0.0")])],"isStart":false});
            var Q36;
            Q36=makeQuery(id+"F8.opExtrude","CAP_EDGE",EDGE,{"disambiguationData":[OSD([sQuery(id+"F7.wireOp",EDGE,"E12.36.0.0")])],"isStart":false});
            var Q37;
            Q37=makeQuery(id+"F8.opExtrude","CAP_EDGE",EDGE,{"disambiguationData":[OSD([sQuery(id+"F7.wireOp",EDGE,"E12.37.0.0")])],"isStart":false});
            var Q38;
            Q38=makeQuery(id+"F8.opExtrude","CAP_EDGE",EDGE,{"disambiguationData":[OSD([sQuery(id+"F7.wireOp",EDGE,"E12.38.0.0")])],"isStart":false});
            var Q39;
            Q39=makeQuery(id+"F8.opExtrude","CAP_EDGE",EDGE,{"disambiguationData":[OSD([sQuery(id+"F7.wireOp",EDGE,"E12.39.0.0")])],"isStart":false});
            var Q40;
            Q40=makeQuery(id+"F8.opExtrude","CAP_EDGE",EDGE,{"disambiguationData":[OSD([sQuery(id+"F7.wireOp",EDGE,"E12.40.0.0")])],"isStart":false});
            var Q41;
            Q41=makeQuery(id+"F8.opExtrude","CAP_EDGE",EDGE,{"disambiguationData":[OSD([sQuery(id+"F7.wireOp",EDGE,"E12.41.0.0")])],"isStart":false});
            fillet(context, id + "F9", {"entities" : qUnion([Q0, Q1, Q2, Q3, Q4, Q5, Q6, Q7, Q8, Q9, Q10, Q11, Q12, Q13, Q14, Q15, Q16, Q17, Q18, Q19, Q20, Q21, Q22, Q23, Q24, Q25, Q26, Q27, Q28, Q29, Q30, Q31, Q32, Q33, Q34, Q35, Q36, Q37, Q38, Q39, Q40, Q41]), "radius" : 1.5 * mm, "tangentPropagation" : true, "allowEdgeOverflow" : false});
        }
    });
